FCSTD DOCUMENT  (FreeCAD 0.20R29410 (Git))
Label: 2
License: All rights reserved
LicenseURL: http://en.wikipedia.org/wiki/All_rights_reserved
objects: Sketcher::SketchObject×1, PartDesign::Line×1, PartDesign::Plane×1, PartDesign::Body×1
note: 4 computed .brp shape members not serialized (recipe doc carries the construction recipe); baked Part::Feature solids carry a one-line shape summary decoded from their .brp

FEATURE [Sketcher::SketchObject] Sketch
  FullyConstrained = true
  MapMode = 5
  Placement = pos=(0,0,0) rot=(1,0,0;1.5708rad)
  Support = -> [XZ_Plane]
  sketch-geometry (1):
    g0: Circle CenterX=0 CenterY=0 CenterZ=0 NormalX=0 NormalY=0 NormalZ=1 AngleXU=0 Radius=5
  constraints (2):
    c: Coincident(g0,g-1)
    c: Diameter(g0) = 10
FEATURE [PartDesign::Line] DatumLine
  AttacherType = Attacher::AttachEngineLine
  Length = 20
  MapMode = 29
  Placement = pos=(0,0,0) rot=(0,0.707107,0.707107;3.14159rad)
  ResizeMode = 0
  Support = -> [Y_Axis]
FEATURE [PartDesign::Plane] DatumPlane
  AttachmentOffset = pos=(0,0,30) rot=(0,1,0;0.523599rad)
  Length = 79.989
  MapMode = 5
  Placement = pos=(0,-30,-6.7e-15) rot=(0.935113,0.250563,0.250563;1.63783rad)
  ResizeMode = 0
  Support = -> [XZ_Plane]
  Width = 61.6877
FEATURE [PartDesign::Body] Body
  Group = -> [Sketch,DatumLine,DatumPlane]
  Origin = -> Origin
